# Revit family: ThinkingWall Acoustic Curve
name_source: partatom
category: Generic Models
units: mm (PartAtom-declared; Revit-internal decimal feet)

## family parameters
Always vertical = Yes
Can host rebar = No
Cut with Voids When Loaded = No
Maintain Annotation Orientation = No
Part Type = Normal
Room Calculation Point = No
Round Connector Dimension = Use Diameter
Shared = No
Work Plane-Based = No

## types (3) — shared parameters
Acoustic Colour = <By Category>
Description = Mobile freestanding acoustic curve screen. Part of the ThinkingWall® range for flexible breakout and meeting spaces.
Manufacturer = Logovisual LTD
Model = ThinkingWall® Acoustic Curve
No of Slat = 29
Plinth Colour = <By Category>
Steel Colour = <By Category>
URL = https://www.logovisual.com
zero-valued in all types: Default Elevation

## per-type parameters (varying)
| type | ThinkingWall Acoustic Curve 30deg | ThinkingWall Acoustic Curve 45deg | ThinkingWall Acoustic Curve 90deg |
| ThinkingWall® Acoustic Curve 30deg | Yes | No | No |
| ThinkingWall® Acoustic Curve 45deg | No | Yes | No |
| ThinkingWall® Acoustic Curve 90deg | No | No | Yes |

## geometry (parser evidence)
native form markers: Sweep x24
no freeform markers — native parametric forms only
